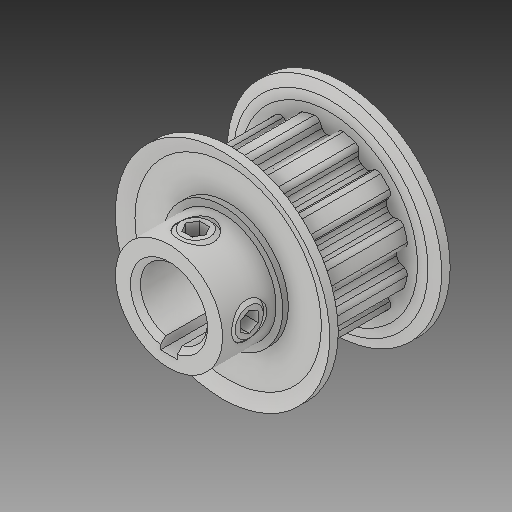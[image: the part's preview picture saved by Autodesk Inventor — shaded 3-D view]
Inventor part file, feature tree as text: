
AUTODESK INVENTOR PART (.ipt)
format: ipt  version: 2018 (Build 220112000, 112)  size: 388,608 bytes
history: native  units: in
note: dims shown in document units (in); Inventor stores cm internally (conversion verified against a paired STEP export)
features: fillet x1
ambient origin geometry x8: Origin, YZ Plane, XZ Plane, XY Plane, X Axis, Y Axis, Z Axis, Center Point
bodies: Solid1 (feature_tree)
feature tree (1):
  fillet  "Fillet2"  [1 undecoded]
note: 1 required parameter value undecoded (feature->parameter linkage not recoverable at this tier; creation-order binding heuristic only, values carry confidence <= 0.55)
